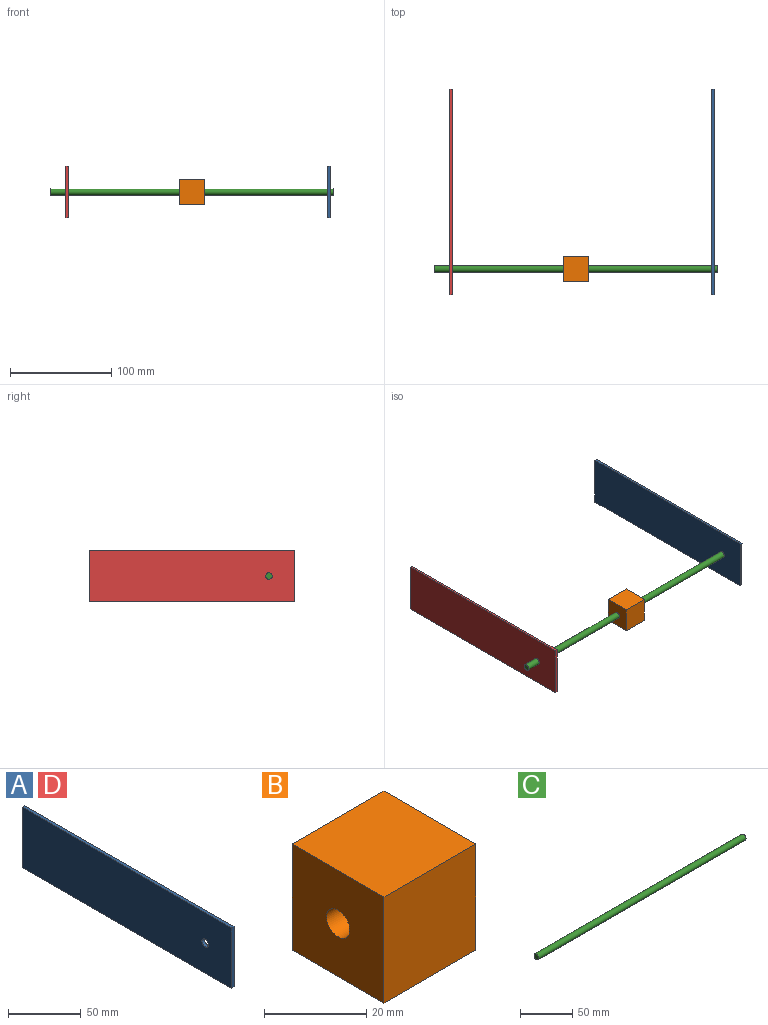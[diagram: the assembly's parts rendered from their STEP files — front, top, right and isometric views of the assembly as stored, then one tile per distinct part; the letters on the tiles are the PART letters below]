
ASSEMBLY  parts=4 mates=6
PART A: 7 faces, bbox 2.5x203.2x50.8 mm
  f0: plane 50.8x2.54mm, normal (0,1,0), area 129mm2, adj f1,f4,f5,f6
  f1: plane 203.2x2.54mm, normal (0,0,1), area 516.1mm2, adj f0,f2,f5,f6
  f2: plane 50.8x2.54mm, normal (0,-1,0), area 129mm2, adj f1,f4,f5,f6
  f3: cylinder r=3.17mm len=6.35mm, axis (-1,0,0), area 50.7mm2, adj f5,f6
  f4: plane 203.2x2.54mm, normal (0,0,-1), area 516.1mm2, adj f0,f2,f5,f6
  f5: plane 203.2x50.8mm, normal (1,0,0), area 10290.9mm2, adj f0,f1,f2,f3,f4
  f6: plane 203.2x50.8mm, normal (-1,0,0), area 10290.9mm2, adj f0,f1,f2,f3,f4
PART B: 7 faces, bbox 25.4x25.4x25.4 mm
  f0: plane 25.4x25.4mm, normal (0,1,0), area 645.2mm2, adj f1,f4,f5,f6
  f1: plane 25.4x25.4mm, normal (0,0,1), area 645.2mm2, adj f0,f2,f5,f6
  f2: plane 25.4x25.4mm, normal (0,-1,0), area 645.2mm2, adj f1,f4,f5,f6
  f3: cylinder r=3.17mm len=25.4mm, axis (-1,0,0), area 506.7mm2, adj f5,f6
  f4: plane 25.4x25.4mm, normal (0,0,-1), area 645.2mm2, adj f0,f2,f5,f6
  f5: plane 25.4x25.4mm, normal (1,0,0), area 613.5mm2, adj f0,f1,f2,f3,f4
  f6: plane 25.4x25.4mm, normal (-1,0,0), area 613.5mm2, adj f0,f1,f2,f3,f4
PART C: 3 faces, bbox 279.4x6.4x6.4 mm
  f0: cylinder r=3.17mm len=279.4mm, axis (-1,0,0), area 5573.8mm2, adj f1,f2
  f1: plane 6.35x6.35mm, normal (1,0,0), area 31.7mm2, adj f0
  f2: plane 6.35x6.35mm, normal (-1,0,0), area 31.7mm2, adj f0
PART D: same geometry as A
PLACE A t=(-114.07,120.56,-133.18)mm
PLACE B rot(axis=(0,0,1),180deg) t=(-235.44,-69.94,-43.57)mm
PLACE C rot(axis=(0,-0.71,0.71),180deg) t=(-108.44,-35.84,22.48)mm
PLACE D rot(axis=(1,0,0),0deg) t=(-372.97,120.56,-133.18)mm
MATE parallel B.f1 <-> A.f1  axis (0,0,1) through (-248.14,-57.24,35.18)mm
MATE cylindrical C.f0 <-> A.f3  axis (1,0,0) through (-108.44,-57.24,22.48)mm
MATE planar C.f0 <-> B.f3  axis (1,0,0) through (-108.44,-57.24,22.48)mm
MATE cylindrical D.f3 <-> C.f0  axis (1,0,0) through (-370.43,-57.24,22.48)mm
MATE cylindrical C.f0 <-> B.f3  axis (1,0,0) through (-387.84,-57.24,22.48)mm
MATE parallel B.f1 <-> D.f1  axis (0,0,1) through (-248.14,-57.24,35.18)mm
